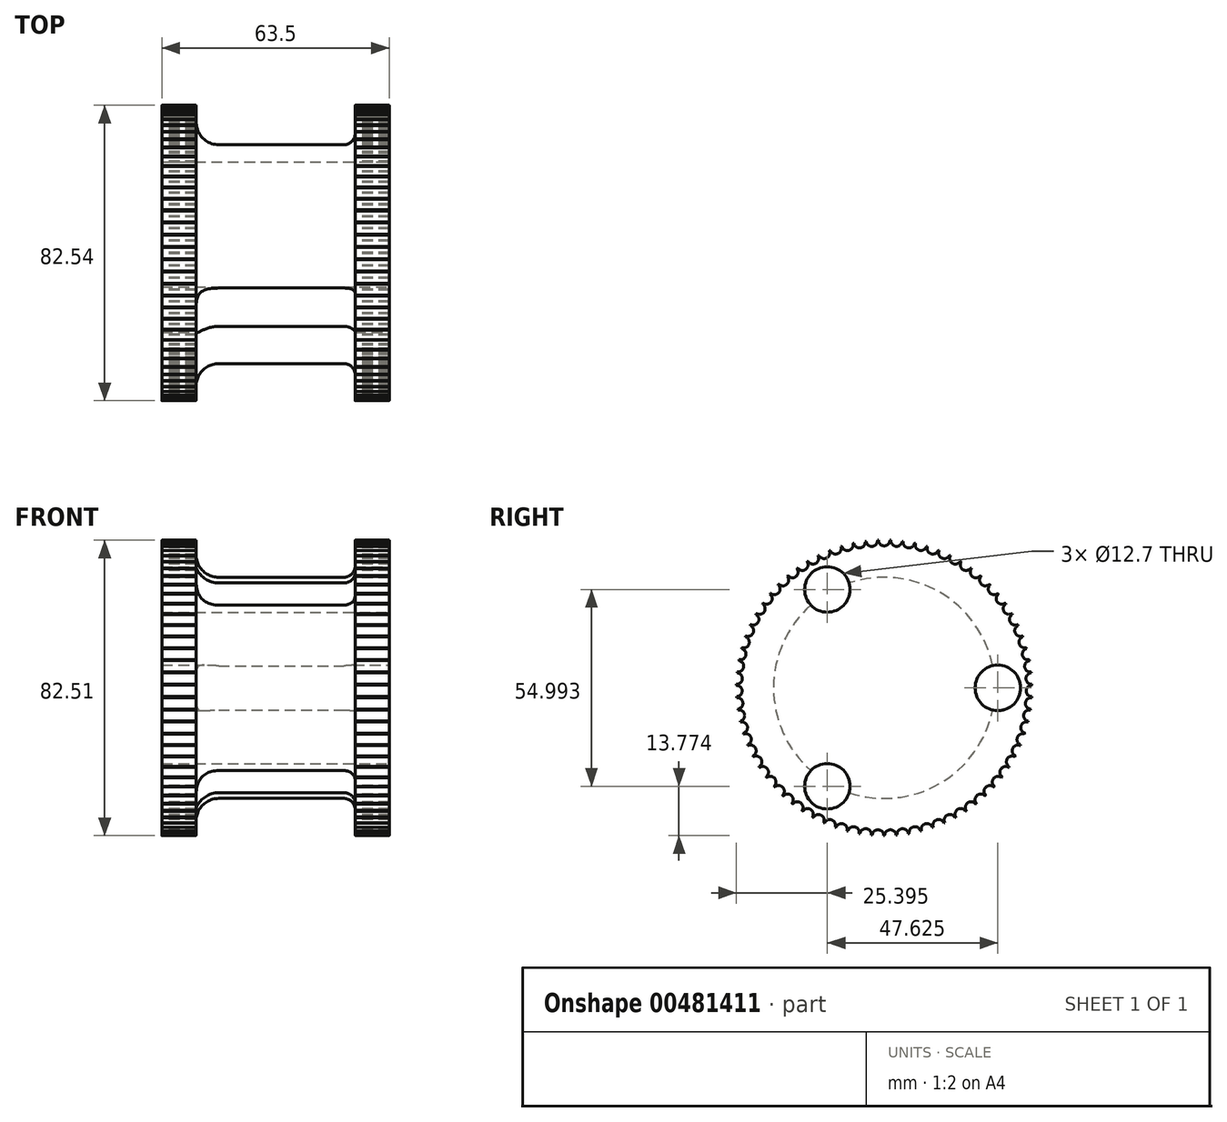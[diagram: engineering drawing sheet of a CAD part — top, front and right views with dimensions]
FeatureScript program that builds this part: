
annotation { "Feature Type Name" : "Feature", "Feature Type Description" : "" }
export const myFeature = defineFeature(function(context is Context, id is Id, definition is map)
    precondition{}
    {
        {
            var Q0;
            Q0=qCreatedBy(makeId("Top.planeOp"),FACE);
            var sketch = newSketch(context, id + "F0", { "sketchPlane" : qUnion([Q0])});
            skLineSegment(sketch, "E0", {"start": v(0, 0) * mm, "end": v(0, 41.28) * mm});
            skLineSegment(sketch, "E1", {"start": v(0, 41.28) * mm, "end": v(9.53, 41.28) * mm});
            skLineSegment(sketch, "E2", {"start": v(9.53, 41.28) * mm, "end": v(9.53, 37.24) * mm});
            skLineSegment(sketch, "E3", {"start": v(15.88, 30.9) * mm, "end": v(50.8, 30.9) * mm});
            skLineSegment(sketch, "E4", {"start": v(53.98, 34.07) * mm, "end": v(53.98, 41.28) * mm});
            skLineSegment(sketch, "E5", {"start": v(53.98, 41.28) * mm, "end": v(63.5, 41.28) * mm});
            skLineSegment(sketch, "E6", {"start": v(63.5, 41.28) * mm, "end": v(63.5, 0) * mm});
            skLineSegment(sketch, "E7", {"start": v(63.5, 0) * mm, "end": v(0, 0) * mm});
            skPoint(sketch, "E8.visualSharp", {"position": v(9.53, 30.9) * mm});
            skArc(sketch, "E8.filletArc", {"start": v(9.53, 37.24) * mm, "mid": v(11.38, 32.75) * mm, "end": v(15.88, 30.9) * mm});
            skPoint(sketch, "E9.visualSharp", {"position": v(53.98, 30.9) * mm});
            skArc(sketch, "E9.filletArc", {"start": v(50.8, 30.9) * mm, "mid": v(53.05, 31.82) * mm, "end": v(53.98, 34.07) * mm});
            skSolve(sketch);
        }
        {
            var Q0;
            Q0=makeQuery(id+"F0.imprint","IMPRINT",FACE,{"disambiguationData":[TD([[makeQuery(id+"F0.imprint","IMPRINT",EDGE,{"derivedFrom":sQuery(id+"F0.wireOp",EDGE,"E0")}),-1.0]])]});
            var Q1;
            Q1=sQuery(id+"F0.wireOp",EDGE,"E7");
            revolve(context, id + "F1", {"entities" : qUnion([Q0]), "axis" : qUnion([Q1]), "revolveType" : RevolveType.FULL});
        }
        {
            var Q0;
            Q0=makeQuery(id+"F1.opRevolve","SWEPT_FACE",FACE,{"disambiguationData":[OSD([sQuery(id+"F0.wireOp",EDGE,"E6")])]});
            var sketch = newSketch(context, id + "F2", { "sketchPlane" : qUnion([Q0])});
            skCircle(sketch, "E10", {"center": v(31.75, 0) * mm, "radius": 6.35 * mm});
            skCircle(sketch, "E11.1.0", {"center": v(-15.88, 27.5) * mm, "radius": 6.35 * mm});
            skCircle(sketch, "E11.2.0", {"center": v(-15.87, -27.5) * mm, "radius": 6.35 * mm});
            skPoint(sketch, "E11.center", {"position": v(0, 0) * mm});
            skLineSegment(sketch, "E11.anchor1", {"start": v(0, 0) * mm, "end": v(31.75, 0) * mm, "construction": true});
            skLineSegment(sketch, "E11.anchor2", {"start": v(0, 0) * mm, "end": v(-15.87, -27.5) * mm, "construction": true});
            skSolve(sketch);
        }
        {
            var Q0;
            Q0=makeQuery(id+"F2.imprint","IMPRINT",FACE,{"disambiguationData":[TD([[makeQuery(id+"F2.imprint","IMPRINT",EDGE,{"derivedFrom":sQuery(id+"F2.wireOp",EDGE,"E11.1.0")}),1.0]])]});
            var Q1;
            Q1=makeQuery(id+"F2.imprint","IMPRINT",FACE,{"disambiguationData":[TD([[makeQuery(id+"F2.imprint","IMPRINT",EDGE,{"derivedFrom":sQuery(id+"F2.wireOp",EDGE,"E11.2.0")}),1.0]])]});
            var Q2;
            Q2=makeQuery(id+"F2.imprint","IMPRINT",FACE,{"disambiguationData":[TD([[makeQuery(id+"F2.imprint","IMPRINT",EDGE,{"derivedFrom":sQuery(id+"F2.wireOp",EDGE,"E10")}),1.0]])]});
            extrude(context, id + "F3", {"entities" : qUnion([Q0, Q1, Q2]), "operationType" : NewBodyOperationType.REMOVE, "oppositeDirection" : true, "depth" : 101.6 * mm});
        }
        {
            var Q0;
            Q0=makeQuery(id+"F1.opRevolve","SWEPT_FACE",FACE,{"disambiguationData":[OSD([sQuery(id+"F0.wireOp",EDGE,"E0")])]});
            var sketch = newSketch(context, id + "F4", { "sketchPlane" : qUnion([Q0])});
            skCircle(sketch, "E12", {"center": v(0, 41.28) * mm, "radius": 1.59 * mm});
            skCircle(sketch, "E13.1.0", {"center": v(-35.75, -20.64) * mm, "radius": 1.59 * mm});
            skCircle(sketch, "E13.2.0", {"center": v(35.75, -20.64) * mm, "radius": 1.59 * mm});
            skPoint(sketch, "E13.center", {"position": v(0, 0) * mm});
            skSolve(sketch);
        }
        {
            var Q0;
            {var subQ0=sQuery(id+"F0.wireOp",EDGE,"E0");var subQ1=makeQuery(id+"F1.opRevolve","SWEPT_FACE",FACE,{"disambiguationData":[OSD([subQ0])]});Q0=makeQuery(id+"F4.imprint","IMPRINT",FACE,{"disambiguationData":[TD([[makeQuery(id+"F4.imprint","IMPRINT",EDGE,{"derivedFrom":makeQuery(id+"F3.boolean.opBoolean","INTERSECT",EDGE,{"derivedFrom":[subQ1,makeQuery(id+"F3.opExtrude","SWEPT_FACE",FACE,{"disambiguationData":[OSD([sQuery(id+"F2.wireOp",EDGE,"E10")])]})]})}),1.0]])]});}
            var sketch = newSketch(context, id + "F5", { "sketchPlane" : qUnion([Q0])});
            skCircle(sketch, "E14", {"center": v(0, 41.28) * mm, "radius": 1.59 * mm});
            skCircle(sketch, "E15.1.0", {"center": v(-3.45, 41.13) * mm, "radius": 1.59 * mm});
            skCircle(sketch, "E15.2.0", {"center": v(-6.88, 40.7) * mm, "radius": 1.59 * mm});
            skCircle(sketch, "E15.3.0", {"center": v(-10.26, 39.98) * mm, "radius": 1.59 * mm});
            skCircle(sketch, "E15.4.0", {"center": v(-13.57, 38.98) * mm, "radius": 1.59 * mm});
            skCircle(sketch, "E15.5.0", {"center": v(-16.79, 37.7) * mm, "radius": 1.59 * mm});
            skCircle(sketch, "E15.6.0", {"center": v(-19.88, 36.17) * mm, "radius": 1.59 * mm});
            skCircle(sketch, "E15.7.0", {"center": v(-22.84, 34.38) * mm, "radius": 1.59 * mm});
            skCircle(sketch, "E15.8.0", {"center": v(-25.64, 32.35) * mm, "radius": 1.59 * mm});
            skCircle(sketch, "E15.9.0", {"center": v(-28.25, 30.09) * mm, "radius": 1.59 * mm});
            skCircle(sketch, "E15.10.0", {"center": v(-30.67, 27.62) * mm, "radius": 1.59 * mm});
            skCircle(sketch, "E15.11.0", {"center": v(-32.88, 24.95) * mm, "radius": 1.59 * mm});
            skCircle(sketch, "E15.12.0", {"center": v(-34.85, 22.12) * mm, "radius": 1.59 * mm});
            skCircle(sketch, "E15.13.0", {"center": v(-36.58, 19.12) * mm, "radius": 1.59 * mm});
            skCircle(sketch, "E15.14.0", {"center": v(-38.05, 16) * mm, "radius": 1.59 * mm});
            skCircle(sketch, "E15.15.0", {"center": v(-39.25, 12.75) * mm, "radius": 1.59 * mm});
            skCircle(sketch, "E15.16.0", {"center": v(-40.18, 9.43) * mm, "radius": 1.59 * mm});
            skCircle(sketch, "E15.17.0", {"center": v(-40.83, 6.03) * mm, "radius": 1.59 * mm});
            skCircle(sketch, "E15.18.0", {"center": v(-41.2, 2.6) * mm, "radius": 1.59 * mm});
            skCircle(sketch, "E15.19.0", {"center": v(-41.27, -0.86) * mm, "radius": 1.59 * mm});
            skCircle(sketch, "E15.20.0", {"center": v(-41.05, -4.31) * mm, "radius": 1.59 * mm});
            skCircle(sketch, "E15.21.0", {"center": v(-40.54, -7.73) * mm, "radius": 1.59 * mm});
            skCircle(sketch, "E15.22.0", {"center": v(-39.75, -11.1) * mm, "radius": 1.59 * mm});
            skCircle(sketch, "E15.23.0", {"center": v(-38.69, -14.39) * mm, "radius": 1.59 * mm});
            skCircle(sketch, "E15.24.0", {"center": v(-37.35, -17.57) * mm, "radius": 1.59 * mm});
            skCircle(sketch, "E15.25.0", {"center": v(-35.75, -20.64) * mm, "radius": 1.59 * mm});
            skCircle(sketch, "E15.26.0", {"center": v(-33.9, -23.56) * mm, "radius": 1.59 * mm});
            skCircle(sketch, "E15.27.0", {"center": v(-31.8, -26.3) * mm, "radius": 1.59 * mm});
            skCircle(sketch, "E15.28.0", {"center": v(-29.49, -28.88) * mm, "radius": 1.59 * mm});
            skCircle(sketch, "E15.29.0", {"center": v(-26.97, -31.24) * mm, "radius": 1.59 * mm});
            skCircle(sketch, "E15.30.0", {"center": v(-24.26, -33.4) * mm, "radius": 1.59 * mm});
            skCircle(sketch, "E15.31.0", {"center": v(-21.38, -35.3) * mm, "radius": 1.59 * mm});
            skCircle(sketch, "E15.32.0", {"center": v(-18.35, -36.97) * mm, "radius": 1.59 * mm});
            skCircle(sketch, "E15.33.0", {"center": v(-15.2, -38.38) * mm, "radius": 1.59 * mm});
            skCircle(sketch, "E15.34.0", {"center": v(-11.93, -39.51) * mm, "radius": 1.59 * mm});
            skCircle(sketch, "E15.35.0", {"center": v(-8.58, -40.37) * mm, "radius": 1.59 * mm});
            skCircle(sketch, "E15.36.0", {"center": v(-5.17, -40.95) * mm, "radius": 1.59 * mm});
            skCircle(sketch, "E15.37.0", {"center": v(-1.73, -41.24) * mm, "radius": 1.59 * mm});
            skCircle(sketch, "E15.38.0", {"center": v(1.73, -41.24) * mm, "radius": 1.59 * mm});
            skCircle(sketch, "E15.39.0", {"center": v(5.17, -40.95) * mm, "radius": 1.59 * mm});
            skCircle(sketch, "E15.40.0", {"center": v(8.58, -40.37) * mm, "radius": 1.59 * mm});
            skCircle(sketch, "E15.41.0", {"center": v(11.93, -39.51) * mm, "radius": 1.59 * mm});
            skCircle(sketch, "E15.42.0", {"center": v(15.2, -38.38) * mm, "radius": 1.59 * mm});
            skCircle(sketch, "E15.43.0", {"center": v(18.35, -36.97) * mm, "radius": 1.59 * mm});
            skCircle(sketch, "E15.44.0", {"center": v(21.38, -35.3) * mm, "radius": 1.59 * mm});
            skCircle(sketch, "E15.45.0", {"center": v(24.26, -33.4) * mm, "radius": 1.59 * mm});
            skCircle(sketch, "E15.46.0", {"center": v(26.97, -31.24) * mm, "radius": 1.59 * mm});
            skCircle(sketch, "E15.47.0", {"center": v(29.49, -28.88) * mm, "radius": 1.59 * mm});
            skCircle(sketch, "E15.48.0", {"center": v(31.8, -26.3) * mm, "radius": 1.59 * mm});
            skCircle(sketch, "E15.49.0", {"center": v(33.9, -23.56) * mm, "radius": 1.59 * mm});
            skCircle(sketch, "E15.50.0", {"center": v(35.75, -20.64) * mm, "radius": 1.59 * mm});
            skCircle(sketch, "E15.51.0", {"center": v(37.35, -17.57) * mm, "radius": 1.59 * mm});
            skCircle(sketch, "E15.52.0", {"center": v(38.69, -14.39) * mm, "radius": 1.59 * mm});
            skCircle(sketch, "E15.53.0", {"center": v(39.75, -11.1) * mm, "radius": 1.59 * mm});
            skCircle(sketch, "E15.54.0", {"center": v(40.54, -7.73) * mm, "radius": 1.59 * mm});
            skCircle(sketch, "E15.55.0", {"center": v(41.05, -4.31) * mm, "radius": 1.59 * mm});
            skCircle(sketch, "E15.56.0", {"center": v(41.27, -0.86) * mm, "radius": 1.59 * mm});
            skCircle(sketch, "E15.57.0", {"center": v(41.2, 2.6) * mm, "radius": 1.59 * mm});
            skCircle(sketch, "E15.58.0", {"center": v(40.83, 6.03) * mm, "radius": 1.59 * mm});
            skCircle(sketch, "E15.59.0", {"center": v(40.18, 9.43) * mm, "radius": 1.59 * mm});
            skCircle(sketch, "E15.60.0", {"center": v(39.25, 12.75) * mm, "radius": 1.59 * mm});
            skCircle(sketch, "E15.61.0", {"center": v(38.05, 16) * mm, "radius": 1.59 * mm});
            skCircle(sketch, "E15.62.0", {"center": v(36.58, 19.12) * mm, "radius": 1.59 * mm});
            skCircle(sketch, "E15.63.0", {"center": v(34.85, 22.12) * mm, "radius": 1.59 * mm});
            skCircle(sketch, "E15.64.0", {"center": v(32.88, 24.95) * mm, "radius": 1.59 * mm});
            skCircle(sketch, "E15.65.0", {"center": v(30.67, 27.62) * mm, "radius": 1.59 * mm});
            skCircle(sketch, "E15.66.0", {"center": v(28.25, 30.09) * mm, "radius": 1.59 * mm});
            skCircle(sketch, "E15.67.0", {"center": v(25.64, 32.35) * mm, "radius": 1.59 * mm});
            skCircle(sketch, "E15.68.0", {"center": v(22.84, 34.38) * mm, "radius": 1.59 * mm});
            skCircle(sketch, "E15.69.0", {"center": v(19.88, 36.17) * mm, "radius": 1.59 * mm});
            skCircle(sketch, "E15.70.0", {"center": v(16.79, 37.7) * mm, "radius": 1.59 * mm});
            skCircle(sketch, "E15.71.0", {"center": v(13.57, 38.98) * mm, "radius": 1.59 * mm});
            skCircle(sketch, "E15.72.0", {"center": v(10.26, 39.98) * mm, "radius": 1.59 * mm});
            skCircle(sketch, "E15.73.0", {"center": v(6.88, 40.7) * mm, "radius": 1.59 * mm});
            skCircle(sketch, "E15.74.0", {"center": v(3.45, 41.13) * mm, "radius": 1.59 * mm});
            skPoint(sketch, "E15.center", {"position": v(0, 0) * mm});
            skSolve(sketch);
        }
        {
            var Q0;
            Q0 = qSketchRegion(id + "F5", true);
            extrude(context, id + "F6", {"entities" : qUnion([Q0]), "operationType" : NewBodyOperationType.REMOVE, "oppositeDirection" : true, "depth" : 101.6 * mm});
        }
    });
